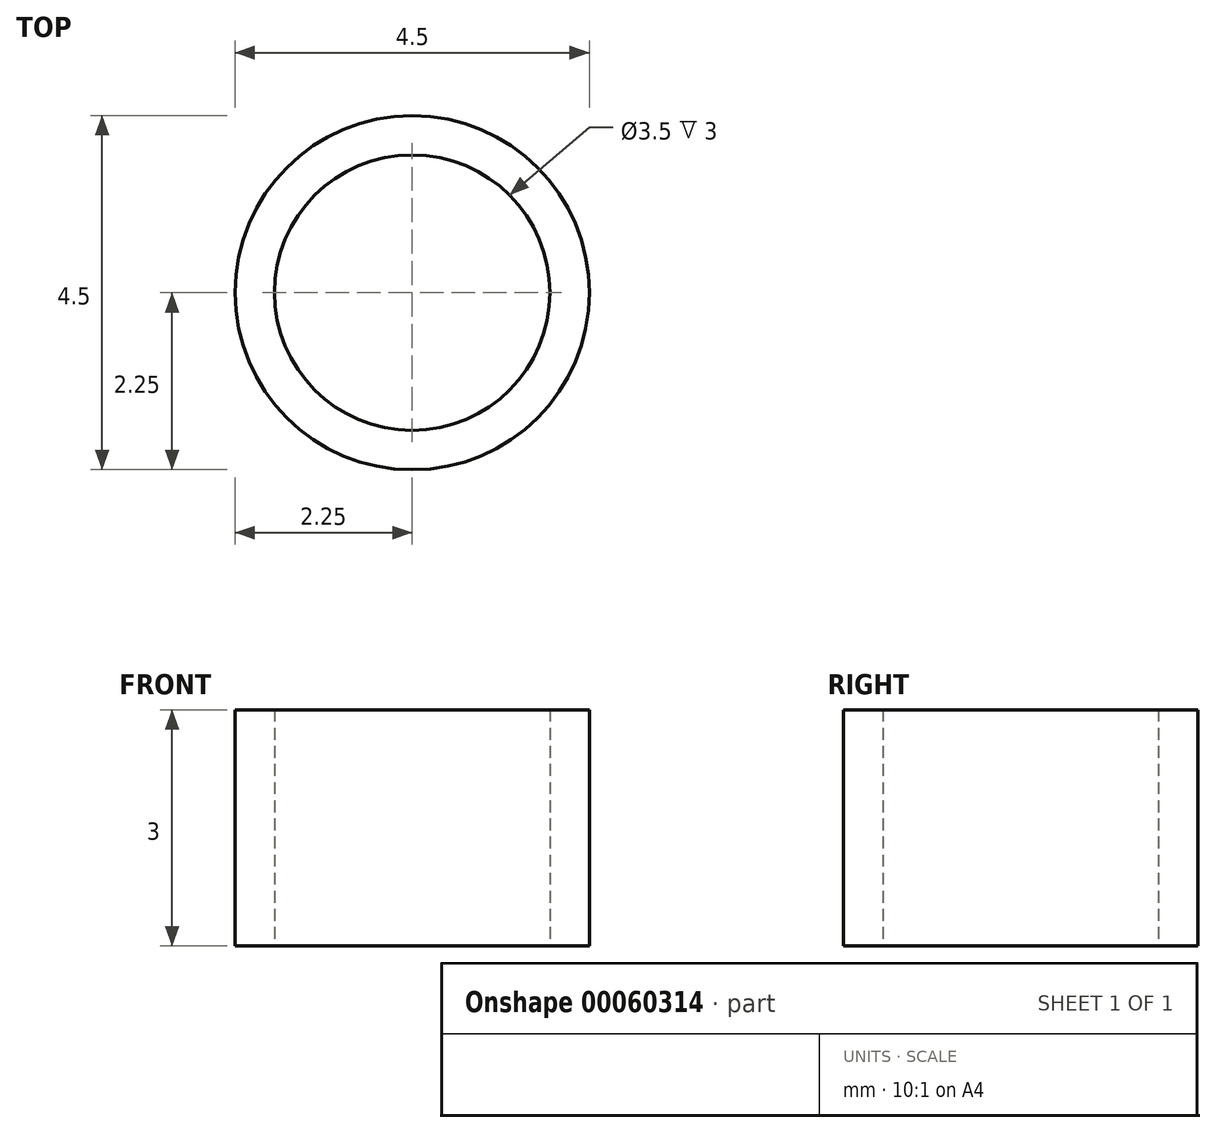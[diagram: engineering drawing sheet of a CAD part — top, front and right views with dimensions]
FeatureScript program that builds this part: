
annotation { "Feature Type Name" : "Feature", "Feature Type Description" : "" }
export const myFeature = defineFeature(function(context is Context, id is Id, definition is map)
    precondition{}
    {
        {
            var Q0;
            Q0=qCreatedBy(makeId("Top.planeOp"),FACE);
            var sketch = newSketch(context, id + "F0", { "sketchPlane" : qUnion([Q0])});
            skCircle(sketch, "E0", {"center": v(0, 0) * mm, "radius": 2.25 * mm});
            skCircle(sketch, "E1", {"center": v(0, 0) * mm, "radius": 1.75 * mm});
            skSolve(sketch);
        }
        {
            var Q0;
            Q0 = qSketchRegion(id + "F0", true);
            extrude(context, id + "F1", {"entities" : qUnion([Q0]), "depth" : 3 * mm});
        }
    });
